# Revit family: FP-Revit20-en-OB30S_Oven-0-US-CA-9000xxxxA
name_source: partatom
category: Specialty Equipment
units: mm (PartAtom-declared; Revit-internal decimal feet)

## family parameters
Always vertical = Yes
Cut with Voids When Loaded = Yes
OmniClass Number = 23.40.40.14.17.11
OmniClass Title = Cookers, Ovens, Stoves
Part Type = Normal
Room Calculation Point = No
Round Connector Dimension = Use Diameter
Shared = No
Work Plane-Based = No

## types (15) — shared parameters
Cavity - Depth = 597 mm
Cavity - Height = 712 mm  [stored 2.33596 ft]
Cavity - Width = 724 mm  [stored 2.37533 ft]
Chassis - Depth = 575 mm
Chassis - Height = 708 mm  [stored 2.32283 ft]
Chassis - Width = 720 mm  [stored 2.3622 ft]
Connector Description - Electrical = 208 or 240 V, 60 Hz, 20 A Service
Manufacturer = Fisher & Paykel Appliances
Material - Clearance Required = Fisher & Paykel - Clearance Required
Opening - Height = 731 mm  [stored 2.39829 ft]
Opening - Width = 762 mm  [stored 2.5 ft]
Product - Height = 729 mm  [stored 2.39173 ft]
Product - Width = 758 mm  [stored 2.48688 ft]
URL = www.fisherpaykel.com
zero-valued in all types: Default Elevation

## per-type parameters (varying)
| type | Control Panel - Depth | Description | Display - Height | Display - Offset | Display - Width | Opening - Depth | Product - Depth | Steam Tank Cut - Depth | Style_ | Type Comments |
| OB30SPPUX3 | 24 mm  [stored 0.0787402 ft] | 30" Self Cleaning Oven | 54 mm  [stored 0.177165 ft] | 23 mm  [stored 0.0754593 ft] | 154 mm  [stored 0.505249 ft] | 24 mm  [stored 0.0787402 ft] | 599 mm  [stored 1.96522 ft] | 10 mm  [stored 0.0328084 ft] | 30in-76cm Fronts : 30in Front Professional | Professional, Stainless |
| OB30SMPUB3 | 20 mm  [stored 0.0656168 ft] | 30" Self Cleaning Oven | 54 mm  [stored 0.177165 ft] | 23 mm  [stored 0.0754593 ft] | 154 mm  [stored 0.505249 ft] | 20 mm  [stored 0.0656168 ft] | 595 mm  [stored 1.9521 ft] | 10 mm  [stored 0.0328084 ft] | 30in-76cm Fronts : 30in Front Minimal (Black) | Minimal, Black |
| OB30SMPUG3 | 20 mm  [stored 0.0656168 ft] | 30" Self Cleaning Oven | 54 mm  [stored 0.177165 ft] | 23 mm  [stored 0.0754593 ft] | 154 mm  [stored 0.505249 ft] | 20 mm  [stored 0.0656168 ft] | 595 mm  [stored 1.9521 ft] | 10 mm  [stored 0.0328084 ft] | 30in-76cm Fronts : 30in Front Minimal (Grey) | Minimal, Grey |
| OB30SMPUNB3 | 20 mm  [stored 0.0656168 ft] | 30" Self Cleaning Oven | 54 mm  [stored 0.177165 ft] | 23 mm  [stored 0.0754593 ft] | 154 mm  [stored 0.505249 ft] | 20 mm  [stored 0.0656168 ft] | 595 mm  [stored 1.9521 ft] | 10 mm  [stored 0.0328084 ft] | 30in-76cm Fronts : 30in Front Minimal (Black) No Handle | Minimal, Black, Handleless |
| OB30SMPUNG3 | 20 mm  [stored 0.0656168 ft] | 30" Self Cleaning Oven | 54 mm  [stored 0.177165 ft] | 23 mm  [stored 0.0754593 ft] | 154 mm  [stored 0.505249 ft] | 20 mm  [stored 0.0656168 ft] | 595 mm  [stored 1.9521 ft] | 10 mm  [stored 0.0328084 ft] | 30in-76cm Fronts : 30in Front Minimal (Grey) No Handle | Minimal, Grey, Handleless |
| OB30SCPUDX3 | 20 mm  [stored 0.0656168 ft] | 30" Self Cleaning Oven | 54 mm  [stored 0.177165 ft] | 23 mm  [stored 0.0754593 ft] | 154 mm  [stored 0.505249 ft] | 20 mm  [stored 0.0656168 ft] | 595 mm  [stored 1.9521 ft] | 10 mm  [stored 0.0328084 ft] | 30in-76cm Fronts : 30in Front Contemporary w Dial (Stainless) | Contemporary, Stainless |
| OB30SCPSUDX3 | 20 mm  [stored 0.0656168 ft] | 30" Self Cleaning Oven, Steam Assist | 54 mm  [stored 0.177165 ft] | 23 mm  [stored 0.0754593 ft] | 154 mm  [stored 0.505249 ft] | 20 mm  [stored 0.0656168 ft] | 595 mm  [stored 1.9521 ft] | 20 mm  [stored 0.0656168 ft] | 30in-76cm Fronts : 30in Front Contemporary w Dial (Stainless) | Contemporary, Stainless |
| OB30SMPSUB3 | 20 mm  [stored 0.0656168 ft] | 30" Self Cleaning Oven, Steam Assist | 54 mm  [stored 0.177165 ft] | 23 mm  [stored 0.0754593 ft] | 154 mm  [stored 0.505249 ft] | 20 mm  [stored 0.0656168 ft] | 595 mm  [stored 1.9521 ft] | 20 mm  [stored 0.0656168 ft] | 30in-76cm Fronts : 30in Front Minimal (Black) | Minimal, Black |
| OB30SMPSUG3 | 20 mm  [stored 0.0656168 ft] | 30" Self Cleaning Oven, Steam Assist | 54 mm  [stored 0.177165 ft] | 23 mm  [stored 0.0754593 ft] | 154 mm  [stored 0.505249 ft] | 20 mm  [stored 0.0656168 ft] | 595 mm  [stored 1.9521 ft] | 20 mm  [stored 0.0656168 ft] | 30in-76cm Fronts : 30in Front Minimal (Grey) | Minimal, Grey |
| OB30SMPSUNB3 | 20 mm  [stored 0.0656168 ft] | 30" Self Cleaning Oven, Steam Assist | 54 mm  [stored 0.177165 ft] | 23 mm  [stored 0.0754593 ft] | 154 mm  [stored 0.505249 ft] | 20 mm  [stored 0.0656168 ft] | 595 mm  [stored 1.9521 ft] | 20 mm  [stored 0.0656168 ft] | 30in-76cm Fronts : 30in Front Minimal (Black) No Handle | Minimal, Black, Handleless |
| OB30SMPSUNG3 | 20 mm  [stored 0.0656168 ft] | 30" Self Cleaning Oven, Steam Assist | 54 mm  [stored 0.177165 ft] | 23 mm  [stored 0.0754593 ft] | 154 mm  [stored 0.505249 ft] | 20 mm  [stored 0.0656168 ft] | 595 mm  [stored 1.9521 ft] | 20 mm  [stored 0.0656168 ft] | 30in-76cm Fronts : 30in Front Minimal (Grey) No Handle | Minimal, Grey, Handleless |
| OB30SPPSUX3 | 24 mm  [stored 0.0787402 ft] | 30" Self Cleaning Oven, Steam Assist | 54 mm  [stored 0.177165 ft] | 23 mm  [stored 0.0754593 ft] | 154 mm  [stored 0.505249 ft] | 24 mm  [stored 0.0787402 ft] | 599 mm  [stored 1.96522 ft] | 23 mm  [stored 0.0754593 ft] | 30in-76cm Fronts : 30in Front Professional | Professional, Stainless |
| OB30SCPTDX3 | 20 mm  [stored 0.0656168 ft] | 30" Self Cleaning Oven | 56 mm  [stored 0.183727 ft] | 26 mm | 108 mm  [stored 0.354331 ft] | 20 mm  [stored 0.0656168 ft] | 595 mm  [stored 1.9521 ft] | 10 mm  [stored 0.0328084 ft] | 30in-76cm Fronts : 30in Front Contemporary w Dial (Stainless) | Contemporary, Stainless, S7 |
| OB30SCPTDB3 | 20 mm  [stored 0.0656168 ft] | 30" Self Cleaning Oven | 56 mm  [stored 0.183727 ft] | 26 mm | 108 mm  [stored 0.354331 ft] | 20 mm  [stored 0.0656168 ft] | 595 mm  [stored 1.9521 ft] | 10 mm  [stored 0.0328084 ft] | 30in-76cm Fronts : 30in Front Contemporary w Dial (Black) | Contemporary, Black, S7 |
| OB30SPPTX3 | 24 mm  [stored 0.0787402 ft] | 30" Self Cleaning Oven | 54 mm  [stored 0.177165 ft] | 23 mm  [stored 0.0754593 ft] | 154 mm  [stored 0.505249 ft] | 24 mm  [stored 0.0787402 ft] | 599 mm  [stored 1.96522 ft] | 10 mm  [stored 0.0328084 ft] | 30in-76cm Fronts : 30in Front Professional | Professional, Stainless, S7 |

note: column(s) folded — value = type name in every type: Model

note: [stored X ft] marks values corroborated as IEEE doubles in the binary element streams (Revit-internal decimal feet)

## geometry (parser evidence)
native form markers: Sweep x16
no freeform markers — native parametric forms only
